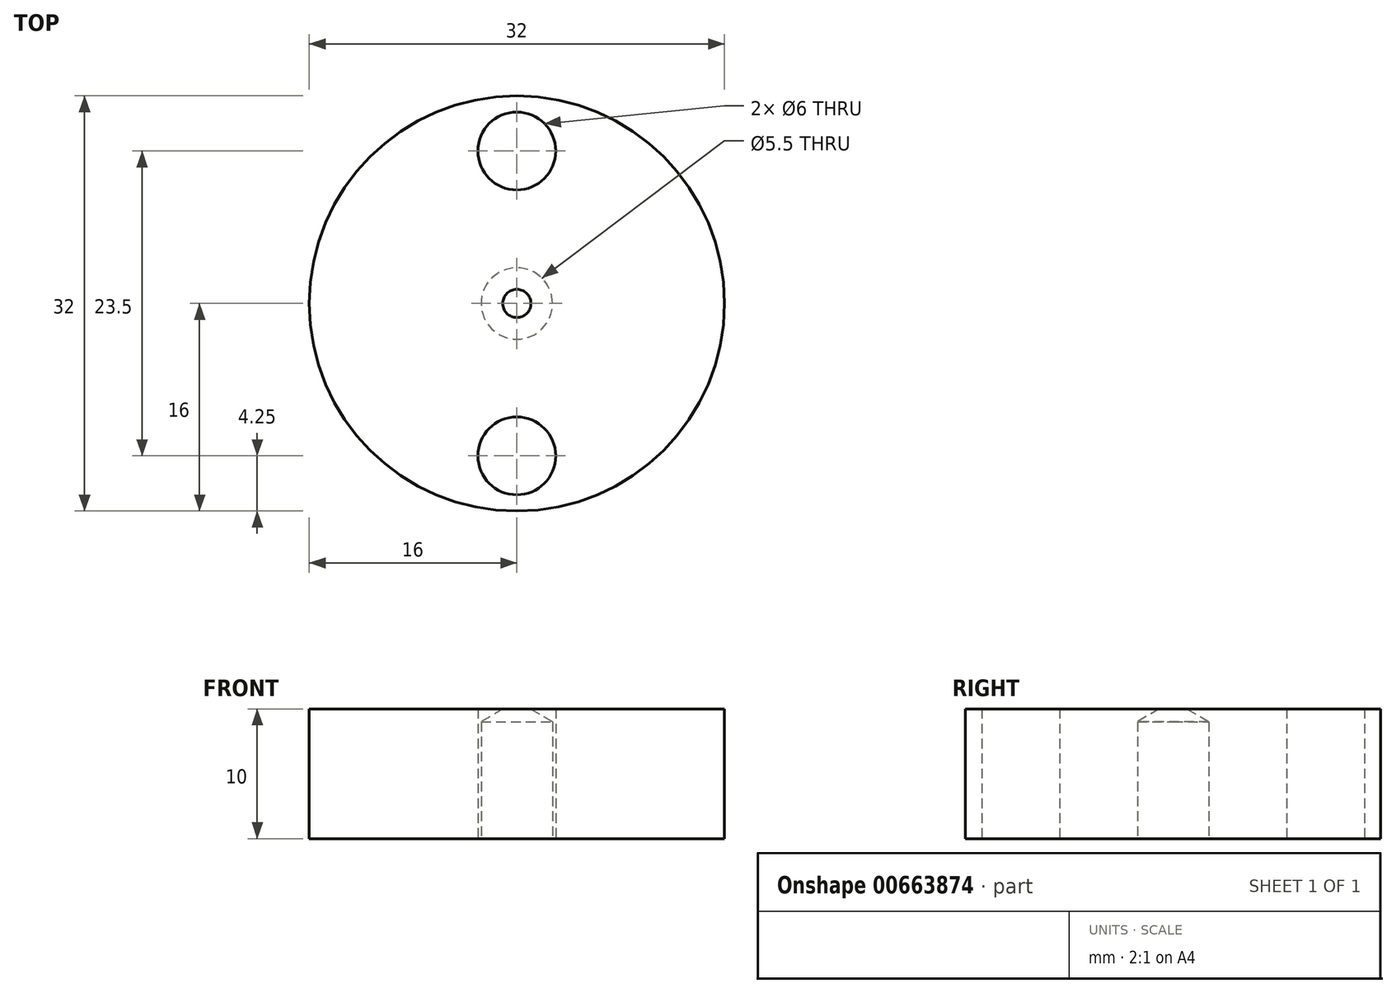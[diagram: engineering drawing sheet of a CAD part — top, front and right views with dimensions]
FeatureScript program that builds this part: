
annotation { "Feature Type Name" : "Feature", "Feature Type Description" : "" }
export const myFeature = defineFeature(function(context is Context, id is Id, definition is map)
    precondition{}
    {
        {
            var Q0;
            Q0=qCreatedBy(makeId("Top.planeOp"),FACE);
            var sketch = newSketch(context, id + "F0", { "sketchPlane" : qUnion([Q0])});
            skCircle(sketch, "E0", {"center": v(0, 0) * mm, "radius": 16 * mm});
            skPoint(sketch, "E1", {"position": v(0, 11.75) * mm});
            skPoint(sketch, "E2", {"position": v(0, -11.75) * mm});
            skCircle(sketch, "E3", {"center": v(0, -11.75) * mm, "radius": 3 * mm});
            skCircle(sketch, "E4", {"center": v(0, 11.75) * mm, "radius": 3 * mm});
            skSolve(sketch);
        }
        {
            var Q0;
            Q0=makeQuery(id+"F0.imprint","IMPRINT",FACE,{"disambiguationData":[TD([[makeQuery(id+"F0.imprint","IMPRINT",EDGE,{"derivedFrom":sQuery(id+"F0.wireOp",EDGE,"E0")}),1.0]])]});
            extrude(context, id + "F1", {"entities" : qUnion([Q0]), "depth" : 10 * mm, "offsetDistance" : 25 * mm});
        }
        {
            var Q0;
            Q0=sQuery(id+"F0.wireOp",VERTEX,"E0.center");
            var Q1;
            Q1=makeQuery(id+"F1.opExtrude","SWEPT_BODY",BODY,{"disambiguationData":[OSD([sQuery(id+"F0.wireOp",EDGE,"E0"),sQuery(id+"F0.wireOp",EDGE,"E3"),sQuery(id+"F0.wireOp",EDGE,"E4")])]});
            hole(context, id + "F2", {"style" : HoleStyle.SIMPLE, "endStyle" : HoleEndStyle.BLIND, "oppositeDirection" : true, "holeDiameter" : 5.5 * mm, "majorDiameter" : 5 * mm, "holeDepth" : 9 * mm, "isTappedThrough" : true, "tappedDepth" : 12 * mm, "tapClearance" : 3, "locations" : qUnion([Q0]), "scope" : qUnion([Q1])});
        }
    });
